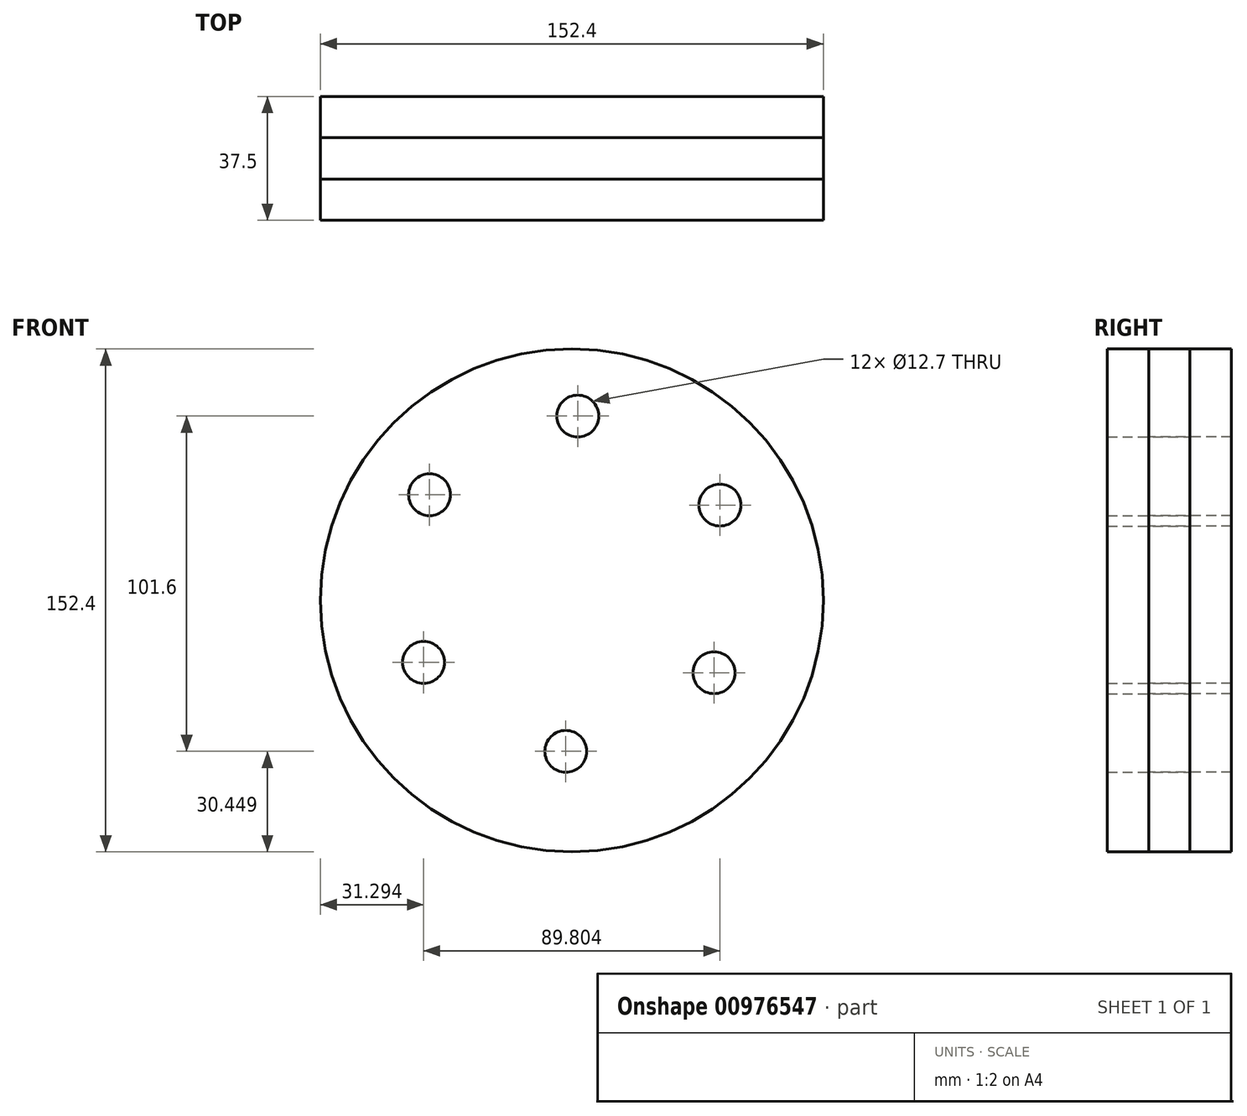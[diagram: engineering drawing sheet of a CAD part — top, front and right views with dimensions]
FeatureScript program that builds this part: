
annotation { "Feature Type Name" : "Feature", "Feature Type Description" : "" }
export const myFeature = defineFeature(function(context is Context, id is Id, definition is map)
    precondition{}
    {
        {
            var Q0;
            Q0=qCreatedBy(makeId("Front.planeOp"),FACE);
            var sketch = newSketch(context, id + "F0", { "sketchPlane" : qUnion([Q0])});
            skCircle(sketch, "E0", {"center": v(43.09, -0.78) * mm, "radius": 76.2 * mm});
            skCircle(sketch, "E1", {"center": v(0, 31.24) * mm, "radius": 6.35 * mm});
            skCircle(sketch, "E2.1.0", {"center": v(-1.82, -19.56) * mm, "radius": 6.35 * mm});
            skCircle(sketch, "E2.2.0", {"center": v(41.27, -46.53) * mm, "radius": 6.35 * mm});
            skPoint(sketch, "E2.center", {"position": v(43.09, 4.27) * mm});
            skCircle(sketch, "E3.1.3.0", {"center": v(86.17, -22.7) * mm, "radius": 6.35 * mm});
            skCircle(sketch, "E3.1.4.0", {"center": v(87.99, 28.1) * mm, "radius": 6.35 * mm});
            skCircle(sketch, "E3.1.5.0", {"center": v(44.9, 55.07) * mm, "radius": 6.35 * mm});
            skSolve(sketch);
        }
        {
            var Q0;
            Q0=qCreatedBy(makeId("Top.planeOp"),FACE);
            var sketch = newSketch(context, id + "F1", { "sketchPlane" : qUnion([Q0])});
            skSolve(sketch);
        }
        {
            var Q0;
            Q0=makeQuery(id+"F0.imprint","IMPRINT",FACE,{"disambiguationData":[TD([[makeQuery(id+"F0.imprint","IMPRINT",EDGE,{"derivedFrom":sQuery(id+"F0.wireOp",EDGE,"E0")}),1.0]])]});
            extrude(context, id + "F2", {"entities" : qUnion([Q0]), "depth" : 25 * mm, "offsetDistance" : 25 * mm});
        }
        {
            var Q0;
            Q0=makeQuery(id+"F2.opExtrude","CAP_FACE",FACE,{"disambiguationData":[OSD([sQuery(id+"F0.wireOp",EDGE,"E0"),sQuery(id+"F0.wireOp",EDGE,"E1"),sQuery(id+"F0.wireOp",EDGE,"E2.1.0"),sQuery(id+"F0.wireOp",EDGE,"E2.2.0"),sQuery(id+"F0.wireOp",EDGE,"E3.1.3.0"),sQuery(id+"F0.wireOp",EDGE,"E3.1.4.0"),sQuery(id+"F0.wireOp",EDGE,"E3.1.5.0")])],"isStart":true});
            var Q1;
            Q1 = qSketchRegion(id + "F1", true);
            extrude(context, id + "F3", {"entities" : qUnion([Q0, Q1]), "depth" : 25 * mm, "offsetDistance" : 25 * mm, "symmetric" : true});
        }
    });
